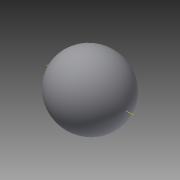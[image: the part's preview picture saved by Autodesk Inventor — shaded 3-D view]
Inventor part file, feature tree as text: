
AUTODESK INVENTOR PART (.ipt)
format: ipt  version: 2015 (Build 190159000, 159)  size: 110,080 bytes
history: native  units: mm
features: revolve x1, sketch x1
ambient origin geometry x8: Origin, YZ Plane, XZ Plane, XY Plane, X Axis, Y Axis, Z Axis, Center Point
bodies: Solid1 (feature_tree)
feature tree (2):
  revolve  "Revolution1"  [1 undecoded]
  sketch  "Sketch1"  dims[d0=90.0deg]
note: 1 required parameter value undecoded (feature->parameter linkage not recoverable at this tier; creation-order binding heuristic only, values carry confidence <= 0.55)
